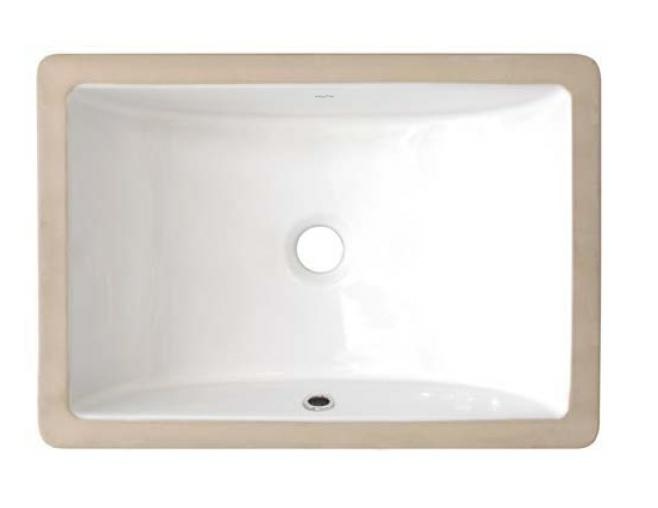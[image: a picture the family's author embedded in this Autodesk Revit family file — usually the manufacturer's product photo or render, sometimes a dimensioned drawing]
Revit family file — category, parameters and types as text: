
# Revit family: HU2014008
name_source: partatom
category: Plumbing Fixtures
revit_build: Autodesk Revit 2016 (Build: 20150220_1215(x64)
units: mm (PartAtom-declared; Revit-internal decimal feet)

## family parameters
Always vertical = Yes
Cut with Voids When Loaded = No
OmniClass Number = 23.45.00.00
OmniClass Title = Sanitary, Laundry, and Cleaning Equipment
Part Type = Normal
Room Calculation Point = No
Round Connector Dimension = Use Diameter
Shared = No
Work Plane-Based = No

## types (1)
- 550 x 350
    Assembly Code = D2010320
    CW Connection = No
    Description = Porcelana vitrificada
    HW Connection = No
    Height = 800 mm  [stored 2.62467 ft]
    Manufacturer = CHC
    Material = Porcelain, Ivory
    Model = HU2014008
    Type Image = HU2014008.jpg
    URL = www.grupochc.cl
    Vent Connection = No
    Waste Connection = Yes

note: [stored X ft] marks values corroborated as IEEE doubles in the binary element streams (Revit-internal decimal feet)

## geometry (parser evidence)
native form markers: Sweep x2
no freeform markers — native parametric forms only
